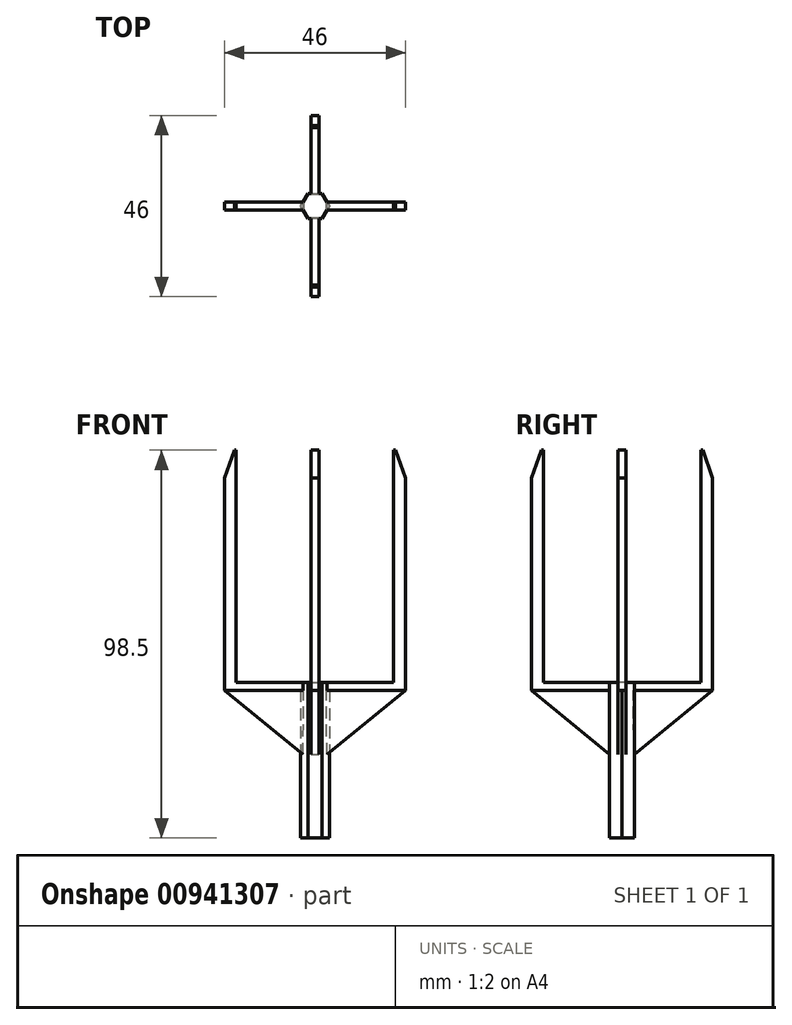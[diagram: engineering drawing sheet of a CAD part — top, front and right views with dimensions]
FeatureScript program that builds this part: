
annotation { "Feature Type Name" : "Feature", "Feature Type Description" : "" }
export const myFeature = defineFeature(function(context is Context, id is Id, definition is map)
    precondition{}
    {
        {
            var Q0;
            Q0=qCreatedBy(makeId("Top.planeOp"),FACE);
            var sketch = newSketch(context, id + "F0", { "sketchPlane" : qUnion([Q0])});
            skCircle(sketch, "E0.cCircle", {"center": v(0, 0) * mm, "radius": 3.15 * mm, "construction": true});
            skLineSegment(sketch, "E0.0", {"start": v(-1.82, 3.15) * mm, "end": v(1.82, 3.15) * mm});
            skLineSegment(sketch, "E0.1", {"start": v(1.82, 3.15) * mm, "end": v(3.64, 0) * mm});
            skLineSegment(sketch, "E0.2", {"start": v(3.64, 0) * mm, "end": v(1.82, -3.15) * mm});
            skLineSegment(sketch, "E0.3", {"start": v(1.82, -3.15) * mm, "end": v(-1.82, -3.15) * mm});
            skLineSegment(sketch, "E0.4", {"start": v(-1.82, -3.15) * mm, "end": v(-3.64, 0) * mm});
            skLineSegment(sketch, "E0.5", {"start": v(-3.64, 0) * mm, "end": v(-1.82, 3.15) * mm});
            skPoint(sketch, "E0.0.midPoint", {"position": v(0, 3.15) * mm});
            skSolve(sketch);
        }
        {
            var Q0;
            Q0=makeQuery(id+"F0.imprint","IMPRINT",FACE,{"disambiguationData":[TD([[makeQuery(id+"F0.imprint","IMPRINT",EDGE,{"derivedFrom":sQuery(id+"F0.wireOp",EDGE,"E0.0")}),-1.0]])]});
            extrude(context, id + "F1", {"entities" : qUnion([Q0]), "depth" : 20 * mm, "offsetDistance" : 25 * mm});
        }
        {
            var Q0;
            Q0=makeQuery(id+"F1.opExtrude","CAP_FACE",FACE,{"disambiguationData":[OSD([sQuery(id+"F0.wireOp",EDGE,"E0.0"),sQuery(id+"F0.wireOp",EDGE,"E0.1"),sQuery(id+"F0.wireOp",EDGE,"E0.2"),sQuery(id+"F0.wireOp",EDGE,"E0.3"),sQuery(id+"F0.wireOp",EDGE,"E0.4"),sQuery(id+"F0.wireOp",EDGE,"E0.5")])],"isStart":false});
            var sketch = newSketch(context, id + "F2", { "sketchPlane" : qUnion([Q0])});
            skLineSegment(sketch, "E1", {"start": v(0, 0) * mm, "end": v(-23, 0) * mm});
            skLineSegment(sketch, "E2", {"start": v(0, 0) * mm, "end": v(21, 0) * mm});
            skLineSegment(sketch, "E3", {"start": v(0, 0) * mm, "end": v(0, 21) * mm});
            skLineSegment(sketch, "E4", {"start": v(0, 0) * mm, "end": v(0, -21) * mm});
            skLineSegment(sketch, "E5.top", {"start": v(0, -1) * mm, "end": v(-23, -1) * mm});
            skLineSegment(sketch, "E5.left", {"start": v(0, 0) * mm, "end": v(0, -1) * mm});
            skLineSegment(sketch, "E5.right", {"start": v(-23, 0) * mm, "end": v(-23, -1) * mm});
            skLineSegment(sketch, "E6.bottom", {"start": v(-23, 0) * mm, "end": v(0, 0) * mm});
            skLineSegment(sketch, "E6.top", {"start": v(-23, 1) * mm, "end": v(0, 1) * mm});
            skLineSegment(sketch, "E6.left", {"start": v(-23, 0) * mm, "end": v(-23, 1) * mm});
            skLineSegment(sketch, "E6.right", {"start": v(0, 0) * mm, "end": v(0, 1) * mm});
            skLineSegment(sketch, "E7.1.0", {"start": v(0, 0) * mm, "end": v(0, -23) * mm});
            skLineSegment(sketch, "E7.1.1", {"start": v(0, -23) * mm, "end": v(-1, -23) * mm});
            skLineSegment(sketch, "E7.1.2", {"start": v(1, 0) * mm, "end": v(1, -23) * mm});
            skLineSegment(sketch, "E7.1.3", {"start": v(0, -23) * mm, "end": v(1, -23) * mm});
            skLineSegment(sketch, "E7.1.4", {"start": v(0, 0) * mm, "end": v(1, 0) * mm});
            skLineSegment(sketch, "E7.1.5", {"start": v(-1, -23) * mm, "end": v(-1, 0) * mm});
            skLineSegment(sketch, "E7.1.6", {"start": v(0, 0) * mm, "end": v(-1, 0) * mm});
            skLineSegment(sketch, "E7.1.7", {"start": v(0, -23) * mm, "end": v(0, 0) * mm});
            skLineSegment(sketch, "E7.1.8", {"start": v(0, 0) * mm, "end": v(0, -23) * mm});
            skLineSegment(sketch, "E7.2.0", {"start": v(0, 0) * mm, "end": v(23, 0) * mm});
            skLineSegment(sketch, "E7.2.1", {"start": v(23, 0) * mm, "end": v(23, -1) * mm});
            skLineSegment(sketch, "E7.2.2", {"start": v(0, 1) * mm, "end": v(23, 1) * mm});
            skLineSegment(sketch, "E7.2.3", {"start": v(23, 0) * mm, "end": v(23, 1) * mm});
            skLineSegment(sketch, "E7.2.5", {"start": v(23, -1) * mm, "end": v(0, -1) * mm});
            skLineSegment(sketch, "E7.2.7", {"start": v(23, 0) * mm, "end": v(0, 0) * mm});
            skLineSegment(sketch, "E7.2.8", {"start": v(0, 0) * mm, "end": v(23, 0) * mm});
            skLineSegment(sketch, "E7.3.0", {"start": v(0, 0) * mm, "end": v(0, 23) * mm});
            skLineSegment(sketch, "E7.3.1", {"start": v(0, 23) * mm, "end": v(1, 23) * mm});
            skLineSegment(sketch, "E7.3.2", {"start": v(-1, 0) * mm, "end": v(-1, 23) * mm});
            skLineSegment(sketch, "E7.3.3", {"start": v(0, 23) * mm, "end": v(-1, 23) * mm});
            skLineSegment(sketch, "E7.3.4", {"start": v(0, 0) * mm, "end": v(-1, 0) * mm});
            skLineSegment(sketch, "E7.3.5", {"start": v(1, 23) * mm, "end": v(1, 0) * mm});
            skLineSegment(sketch, "E7.3.6", {"start": v(0, 0) * mm, "end": v(1, 0) * mm});
            skLineSegment(sketch, "E7.3.7", {"start": v(0, 23) * mm, "end": v(0, 0) * mm});
            skLineSegment(sketch, "E7.3.8", {"start": v(0, 0) * mm, "end": v(0, 23) * mm});
            skPoint(sketch, "E7.center", {"position": v(0, 0) * mm});
            skSolve(sketch);
        }
        {
            var Q0;
            {var subQ4=sQuery(id+"F2.wireOp",EDGE,"E7.3.0");Q0=makeQuery(id+"F2.imprint","IMPRINT",FACE,{"disambiguationData":[TD([[makeQuery(id+"F2.imprint","IMPRINT",EDGE,{"derivedFrom":subQ4}),-1.0]])]});}
            var Q1;
            {var subQ4=sQuery(id+"F2.wireOp",EDGE,"E7.3.0");Q1=makeQuery(id+"F2.imprint","IMPRINT",FACE,{"disambiguationData":[TD([[makeQuery(id+"F2.imprint","IMPRINT",EDGE,{"derivedFrom":subQ4}),1.0]])]});}
            var Q2;
            {var subQ4=sQuery(id+"F2.wireOp",EDGE,"E7.2.0");Q2=makeQuery(id+"F2.imprint","IMPRINT",FACE,{"disambiguationData":[TD([[makeQuery(id+"F2.imprint","IMPRINT",EDGE,{"derivedFrom":subQ4}),1.0]])]});}
            var Q3;
            {var subQ6=sQuery(id+"F2.wireOp",EDGE,"E7.2.0");Q3=makeQuery(id+"F2.imprint","IMPRINT",FACE,{"disambiguationData":[TD([[makeQuery(id+"F2.imprint","IMPRINT",EDGE,{"derivedFrom":subQ6}),-1.0]])]});}
            var Q4;
            {var subQ4=sQuery(id+"F2.wireOp",EDGE,"E7.1.0");Q4=makeQuery(id+"F2.imprint","IMPRINT",FACE,{"disambiguationData":[TD([[makeQuery(id+"F2.imprint","IMPRINT",EDGE,{"derivedFrom":subQ4}),1.0]])]});}
            var Q5;
            {var subQ4=sQuery(id+"F2.wireOp",EDGE,"E7.1.0");Q5=makeQuery(id+"F2.imprint","IMPRINT",FACE,{"disambiguationData":[TD([[makeQuery(id+"F2.imprint","IMPRINT",EDGE,{"derivedFrom":subQ4}),-1.0]])]});}
            var Q6;
            {var subQ3=sQuery(id+"F2.wireOp",EDGE,"E6.left");Q6=makeQuery(id+"F2.imprint","IMPRINT",FACE,{"disambiguationData":[TD([[makeQuery(id+"F2.imprint","IMPRINT",EDGE,{"derivedFrom":subQ3}),-1.0]])]});}
            var Q7;
            {var subQ3=sQuery(id+"F2.wireOp",EDGE,"E5.right");Q7=makeQuery(id+"F2.imprint","IMPRINT",FACE,{"disambiguationData":[TD([[makeQuery(id+"F2.imprint","IMPRINT",EDGE,{"derivedFrom":subQ3}),1.0]])]});}
            var Q8;
            {var subQ0=sQuery(id+"F2.wireOp",EDGE,"E7.3.2");var subQ1=sQuery(id+"F2.wireOp",EDGE,"E6.top");var subQ2=makeQuery(id+"F2.imprint","INTERSECT",VERTEX,{"derivedFrom":[subQ1,subQ0]});Q8=makeQuery(id+"F2.imprint","IMPRINT",FACE,{"disambiguationData":[TD([[makeQuery(id+"F2.imprint","IMPRINT",EDGE,{"disambiguationData":[TD([[subQ2,1.0]])],"derivedFrom":subQ1}),1.0]])]});}
            var Q9;
            {var subQ0=sQuery(id+"F2.wireOp",EDGE,"E6.top");var subQ5=sQuery(id+"F2.wireOp",EDGE,"E7.3.2");var subQ6=makeQuery(id+"F2.imprint","INTERSECT",VERTEX,{"derivedFrom":[subQ0,subQ5]});Q9=makeQuery(id+"F2.imprint","IMPRINT",FACE,{"disambiguationData":[TD([[makeQuery(id+"F2.imprint","IMPRINT",EDGE,{"disambiguationData":[TD([[subQ6,-1.0]])],"derivedFrom":subQ5}),-1.0]])]});}
            var Q10;
            {var subQ0=sQuery(id+"F2.wireOp",EDGE,"E7.2.2");var subQ5=sQuery(id+"F2.wireOp",EDGE,"E7.3.5");var subQ6=makeQuery(id+"F2.imprint","INTERSECT",VERTEX,{"derivedFrom":[subQ0,subQ5]});Q10=makeQuery(id+"F2.imprint","IMPRINT",FACE,{"disambiguationData":[TD([[makeQuery(id+"F2.imprint","IMPRINT",EDGE,{"disambiguationData":[TD([[subQ6,1.0]])],"derivedFrom":subQ5}),-1.0]])]});}
            var Q11;
            {var subQ0=sQuery(id+"F2.wireOp",EDGE,"E7.3.5");var subQ1=sQuery(id+"F2.wireOp",EDGE,"E7.2.2");var subQ2=makeQuery(id+"F2.imprint","INTERSECT",VERTEX,{"derivedFrom":[subQ1,subQ0]});Q11=makeQuery(id+"F2.imprint","IMPRINT",FACE,{"disambiguationData":[TD([[makeQuery(id+"F2.imprint","IMPRINT",EDGE,{"disambiguationData":[TD([[subQ2,-1.0]])],"derivedFrom":subQ1}),1.0]])]});}
            var Q12;
            {var subQ3=sQuery(id+"F2.wireOp",EDGE,"E7.3.5");var subQ5=sQuery(id+"F2.wireOp",EDGE,"E7.2.2");var subQ6=makeQuery(id+"F2.imprint","INTERSECT",VERTEX,{"derivedFrom":[subQ5,subQ3]});Q12=makeQuery(id+"F2.imprint","IMPRINT",FACE,{"disambiguationData":[TD([[makeQuery(id+"F2.imprint","IMPRINT",EDGE,{"disambiguationData":[TD([[subQ6,-1.0]])],"derivedFrom":subQ5}),-1.0]])]});}
            var Q13;
            {var subQ3=sQuery(id+"F2.wireOp",EDGE,"E7.1.2");var subQ5=sQuery(id+"F2.wireOp",EDGE,"E7.2.5");var subQ6=makeQuery(id+"F2.imprint","INTERSECT",VERTEX,{"derivedFrom":[subQ3,subQ5]});Q13=makeQuery(id+"F2.imprint","IMPRINT",FACE,{"disambiguationData":[TD([[makeQuery(id+"F2.imprint","IMPRINT",EDGE,{"disambiguationData":[TD([[subQ6,1.0]])],"derivedFrom":subQ5}),-1.0]])]});}
            var Q14;
            {var subQ0=sQuery(id+"F2.wireOp",EDGE,"E7.2.5");var subQ1=sQuery(id+"F2.wireOp",EDGE,"E7.1.2");var subQ2=makeQuery(id+"F2.imprint","INTERSECT",VERTEX,{"derivedFrom":[subQ1,subQ0]});Q14=makeQuery(id+"F2.imprint","IMPRINT",FACE,{"disambiguationData":[TD([[makeQuery(id+"F2.imprint","IMPRINT",EDGE,{"disambiguationData":[TD([[subQ2,-1.0]])],"derivedFrom":subQ1}),1.0]])]});}
            var Q15;
            {var subQ0=sQuery(id+"F2.wireOp",EDGE,"E7.2.5");var subQ5=sQuery(id+"F2.wireOp",EDGE,"E7.1.2");var subQ6=makeQuery(id+"F2.imprint","INTERSECT",VERTEX,{"derivedFrom":[subQ5,subQ0]});Q15=makeQuery(id+"F2.imprint","IMPRINT",FACE,{"disambiguationData":[TD([[makeQuery(id+"F2.imprint","IMPRINT",EDGE,{"disambiguationData":[TD([[subQ6,-1.0]])],"derivedFrom":subQ5}),-1.0]])]});}
            var Q16;
            {var subQ0=sQuery(id+"F2.wireOp",EDGE,"E5.top");var subQ5=sQuery(id+"F2.wireOp",EDGE,"E7.1.5");var subQ6=makeQuery(id+"F2.imprint","INTERSECT",VERTEX,{"derivedFrom":[subQ0,subQ5]});Q16=makeQuery(id+"F2.imprint","IMPRINT",FACE,{"disambiguationData":[TD([[makeQuery(id+"F2.imprint","IMPRINT",EDGE,{"disambiguationData":[TD([[subQ6,1.0]])],"derivedFrom":subQ5}),-1.0]])]});}
            var Q17;
            {var subQ0=sQuery(id+"F2.wireOp",EDGE,"E7.1.5");var subQ1=sQuery(id+"F2.wireOp",EDGE,"E5.top");var subQ2=makeQuery(id+"F2.imprint","INTERSECT",VERTEX,{"derivedFrom":[subQ1,subQ0]});Q17=makeQuery(id+"F2.imprint","IMPRINT",FACE,{"disambiguationData":[TD([[makeQuery(id+"F2.imprint","IMPRINT",EDGE,{"disambiguationData":[TD([[subQ2,-1.0]])],"derivedFrom":subQ1}),1.0]])]});}
            var Q18;
            {var subQ3=sQuery(id+"F2.wireOp",EDGE,"E7.1.5");var subQ5=sQuery(id+"F2.wireOp",EDGE,"E5.top");var subQ6=makeQuery(id+"F2.imprint","INTERSECT",VERTEX,{"derivedFrom":[subQ5,subQ3]});Q18=makeQuery(id+"F2.imprint","IMPRINT",FACE,{"disambiguationData":[TD([[makeQuery(id+"F2.imprint","IMPRINT",EDGE,{"disambiguationData":[TD([[subQ6,-1.0]])],"derivedFrom":subQ5}),-1.0]])]});}
            var Q19;
            {var subQ3=sQuery(id+"F2.wireOp",EDGE,"E7.3.2");var subQ5=sQuery(id+"F2.wireOp",EDGE,"E6.top");var subQ6=makeQuery(id+"F2.imprint","INTERSECT",VERTEX,{"derivedFrom":[subQ5,subQ3]});Q19=makeQuery(id+"F2.imprint","IMPRINT",FACE,{"disambiguationData":[TD([[makeQuery(id+"F2.imprint","IMPRINT",EDGE,{"disambiguationData":[TD([[subQ6,1.0]])],"derivedFrom":subQ5}),-1.0]])]});}
            var Q20;
            {var subQ0=sQuery(id+"F2.wireOp",EDGE,"E7.3.2");var subQ5=sQuery(id+"F2.wireOp",EDGE,"E6.top");var subQ7=makeQuery(id+"F2.imprint","INTERSECT",VERTEX,{"derivedFrom":[subQ5,subQ0]});Q20=makeQuery(id+"F2.imprint","IMPRINT",FACE,{"disambiguationData":[TD([[makeQuery(id+"F2.imprint","IMPRINT",EDGE,{"disambiguationData":[TD([[subQ7,-1.0]])],"derivedFrom":subQ5}),-1.0]])]});}
            var Q21;
            {var subQ0=sQuery(id+"F2.wireOp",EDGE,"E7.3.5");var subQ5=sQuery(id+"F2.wireOp",EDGE,"E7.2.2");var subQ6=makeQuery(id+"F2.imprint","INTERSECT",VERTEX,{"derivedFrom":[subQ5,subQ0]});Q21=makeQuery(id+"F2.imprint","IMPRINT",FACE,{"disambiguationData":[TD([[makeQuery(id+"F2.imprint","IMPRINT",EDGE,{"disambiguationData":[TD([[subQ6,1.0]])],"derivedFrom":subQ5}),-1.0]])]});}
            var Q22;
            {var subQ0=sQuery(id+"F2.wireOp",EDGE,"E7.1.2");var subQ5=sQuery(id+"F2.wireOp",EDGE,"E7.2.5");var subQ7=makeQuery(id+"F2.imprint","INTERSECT",VERTEX,{"derivedFrom":[subQ0,subQ5]});Q22=makeQuery(id+"F2.imprint","IMPRINT",FACE,{"disambiguationData":[TD([[makeQuery(id+"F2.imprint","IMPRINT",EDGE,{"disambiguationData":[TD([[subQ7,1.0]])],"derivedFrom":subQ0}),-1.0]])]});}
            var Q23;
            {var subQ0=sQuery(id+"F2.wireOp",EDGE,"E7.1.5");var subQ5=sQuery(id+"F2.wireOp",EDGE,"E5.top");var subQ6=makeQuery(id+"F2.imprint","INTERSECT",VERTEX,{"derivedFrom":[subQ5,subQ0]});Q23=makeQuery(id+"F2.imprint","IMPRINT",FACE,{"disambiguationData":[TD([[makeQuery(id+"F2.imprint","IMPRINT",EDGE,{"disambiguationData":[TD([[subQ6,1.0]])],"derivedFrom":subQ5}),-1.0]])]});}
            extrude(context, id + "F3", {"entities" : qUnion([Q0, Q1, Q2, Q3, Q4, Q5, Q6, Q7, Q8, Q9, Q10, Q11, Q12, Q13, Q14, Q15, Q16, Q17, Q18, Q19, Q20, Q21, Q22, Q23]), "operationType" : NewBodyOperationType.ADD, "depth" : 2 * mm, "offsetDistance" : 25 * mm});
        }
        {
            var Q0;
            Q0=makeQuery(id+"F3.opExtrude","CAP_FACE",FACE,{"disambiguationData":[OSD([sQuery(id+"F0.wireOp",EDGE,"E0.0"),sQuery(id+"F0.wireOp",EDGE,"E0.1"),sQuery(id+"F0.wireOp",EDGE,"E0.2"),sQuery(id+"F0.wireOp",EDGE,"E0.3"),sQuery(id+"F0.wireOp",EDGE,"E0.4"),sQuery(id+"F0.wireOp",EDGE,"E0.5"),sQuery(id+"F2.wireOp",EDGE,"E5.top"),sQuery(id+"F2.wireOp",EDGE,"E5.right"),sQuery(id+"F2.wireOp",EDGE,"E6.top"),sQuery(id+"F2.wireOp",EDGE,"E6.left"),sQuery(id+"F2.wireOp",EDGE,"E7.1.1"),sQuery(id+"F2.wireOp",EDGE,"E7.1.2"),sQuery(id+"F2.wireOp",EDGE,"E7.1.3"),sQuery(id+"F2.wireOp",EDGE,"E7.1.5"),sQuery(id+"F2.wireOp",EDGE,"E7.2.1"),sQuery(id+"F2.wireOp",EDGE,"E7.2.2"),sQuery(id+"F2.wireOp",EDGE,"E7.2.3"),sQuery(id+"F2.wireOp",EDGE,"E7.2.5"),sQuery(id+"F2.wireOp",EDGE,"E7.3.1"),sQuery(id+"F2.wireOp",EDGE,"E7.3.2"),sQuery(id+"F2.wireOp",EDGE,"E7.3.3"),sQuery(id+"F2.wireOp",EDGE,"E7.3.5")])],"isStart":false});
            var sketch = newSketch(context, id + "F4", { "sketchPlane" : qUnion([Q0])});
            skLineSegment(sketch, "E8.bottom", {"start": v(-23, 1) * mm, "end": v(-20, 1) * mm});
            skLineSegment(sketch, "E8.top", {"start": v(-23, -1) * mm, "end": v(-20, -1) * mm});
            skLineSegment(sketch, "E8.left", {"start": v(-23, 1) * mm, "end": v(-23, -1) * mm});
            skLineSegment(sketch, "E8.right", {"start": v(-20, 1) * mm, "end": v(-20, -1) * mm});
            skLineSegment(sketch, "E9.bottom", {"start": v(-1, -23) * mm, "end": v(1, -23) * mm});
            skLineSegment(sketch, "E9.top", {"start": v(-1, -20) * mm, "end": v(1, -20) * mm});
            skLineSegment(sketch, "E9.left", {"start": v(-1, -23) * mm, "end": v(-1, -20) * mm});
            skLineSegment(sketch, "E9.right", {"start": v(1, -23) * mm, "end": v(1, -20) * mm});
            skLineSegment(sketch, "E10.bottom", {"start": v(23, 1) * mm, "end": v(20, 1) * mm});
            skLineSegment(sketch, "E10.top", {"start": v(23, -1) * mm, "end": v(20, -1) * mm});
            skLineSegment(sketch, "E10.left", {"start": v(23, 1) * mm, "end": v(23, -1) * mm});
            skLineSegment(sketch, "E10.right", {"start": v(20, 1) * mm, "end": v(20, -1) * mm});
            skLineSegment(sketch, "E11.bottom", {"start": v(-1, 23) * mm, "end": v(1, 23) * mm});
            skLineSegment(sketch, "E11.top", {"start": v(-1, 20) * mm, "end": v(1, 20) * mm});
            skLineSegment(sketch, "E11.left", {"start": v(-1, 23) * mm, "end": v(-1, 20) * mm});
            skLineSegment(sketch, "E11.right", {"start": v(1, 23) * mm, "end": v(1, 20) * mm});
            skSolve(sketch);
        }
        {
            var Q0;
            Q0=makeQuery(id+"F4.imprint","IMPRINT",FACE,{"disambiguationData":[TD([[makeQuery(id+"F4.imprint","IMPRINT",EDGE,{"derivedFrom":sQuery(id+"F4.wireOp",EDGE,"E11.bottom")}),-1.0]])]});
            var Q1;
            Q1=makeQuery(id+"F4.imprint","IMPRINT",FACE,{"disambiguationData":[TD([[makeQuery(id+"F4.imprint","IMPRINT",EDGE,{"derivedFrom":sQuery(id+"F4.wireOp",EDGE,"E8.bottom")}),-1.0]])]});
            var Q2;
            Q2=makeQuery(id+"F4.imprint","IMPRINT",FACE,{"disambiguationData":[TD([[makeQuery(id+"F4.imprint","IMPRINT",EDGE,{"derivedFrom":sQuery(id+"F4.wireOp",EDGE,"E10.bottom")}),-1.0]])]});
            var Q3;
            Q3=makeQuery(id+"F4.imprint","IMPRINT",FACE,{"disambiguationData":[TD([[makeQuery(id+"F4.imprint","IMPRINT",EDGE,{"derivedFrom":sQuery(id+"F4.wireOp",EDGE,"E9.bottom")}),1.0]])]});
            extrude(context, id + "F5", {"entities" : qUnion([Q0, Q1, Q2, Q3]), "operationType" : NewBodyOperationType.ADD, "depth" : 59 * mm, "offsetDistance" : 25 * mm});
        }
        {
            var Q0;
            Q0=makeQuery(id+"F5.opExtrude","CAP_EDGE",EDGE,{"disambiguationData":[OSD([sQuery(id+"F4.wireOp",EDGE,"E11.bottom")])],"isStart":false});
            var Q1;
            Q1=makeQuery(id+"F5.opExtrude","CAP_EDGE",EDGE,{"disambiguationData":[OSD([sQuery(id+"F4.wireOp",EDGE,"E8.left")])],"isStart":false});
            chamfer(context, id + "F6", {"entities" : qUnion([Q0, Q1]), "chamferType" : ChamferType.TWO_OFFSETS, "width1" : 7 * mm, "oppositeDirection" : false, "width2" : 2.5 * mm, "tangentPropagation" : true});
        }
        {
            var Q0;
            Q0=makeQuery(id+"F5.opExtrude","CAP_EDGE",EDGE,{"disambiguationData":[OSD([sQuery(id+"F4.wireOp",EDGE,"E9.bottom")])],"isStart":false});
            var Q1;
            Q1=makeQuery(id+"F5.opExtrude","CAP_EDGE",EDGE,{"disambiguationData":[OSD([sQuery(id+"F4.wireOp",EDGE,"E10.left")])],"isStart":false});
            chamfer(context, id + "F7", {"entities" : qUnion([Q0, Q1]), "chamferType" : ChamferType.TWO_OFFSETS, "width1" : 2.5 * mm, "oppositeDirection" : false, "width2" : 7 * mm, "tangentPropagation" : true});
        }
        {
            var Q0;
            Q0=makeQuery(id+"F5.boolean.opBoolean","MERGE",FACE,{"derivedFrom":[makeQuery(id+"F3.opExtrude","SWEPT_FACE",FACE,{"disambiguationData":[OSD([sQuery(id+"F2.wireOp",EDGE,"E7.1.2")])]}),makeQuery(id+"F5.opExtrude","SWEPT_FACE",FACE,{"disambiguationData":[OSD([sQuery(id+"F4.wireOp",EDGE,"E9.right")])]})]});
            var sketch = newSketch(context, id + "F8", { "sketchPlane" : qUnion([Q0])});
            skLineSegment(sketch, "E12", {"start": v(-23, 20) * mm, "end": v(-3.03, 3.67) * mm});
            skLineSegment(sketch, "E13", {"start": v(-3.03, 3.67) * mm, "end": v(-2.89, 20) * mm});
            skLineSegment(sketch, "E14", {"start": v(-2.89, 20) * mm, "end": v(-23, 20) * mm});
            skSolve(sketch);
        }
        {
            var Q0;
            {var subQ0=sQuery(id+"F8.wireOp",EDGE,"E12");Q0=makeQuery(id+"F8.imprint","IMPRINT",FACE,{"disambiguationData":[TD([[makeQuery(id+"F8.imprint","IMPRINT",EDGE,{"derivedFrom":subQ0}),1.0]])]});}
            extrude(context, id + "F9", {"entities" : qUnion([Q0]), "oppositeDirection" : true, "depth" : 2 * mm, "offsetDistance" : 25 * mm});
        }
        {
            var Q0;
            Q0=makeQuery(id+"F1.opExtrude","CAP_FACE",FACE,{"disambiguationData":[OSD([sQuery(id+"F0.wireOp",EDGE,"E0.0"),sQuery(id+"F0.wireOp",EDGE,"E0.1"),sQuery(id+"F0.wireOp",EDGE,"E0.2"),sQuery(id+"F0.wireOp",EDGE,"E0.3"),sQuery(id+"F0.wireOp",EDGE,"E0.4"),sQuery(id+"F0.wireOp",EDGE,"E0.5")])],"isStart":true});
            extrude(context, id + "F10", {"entities" : qUnion([Q0]), "operationType" : NewBodyOperationType.ADD, "depth" : 17.5 * mm, "offsetDistance" : 25 * mm});
        }
        {
            var Q0;
            Q0=qCreatedBy(makeId("Right.planeOp"),FACE);
            var sketch = newSketch(context, id + "F11", { "sketchPlane" : qUnion([Q0])});
            skLineSegment(sketch, "E15", {"start": v(0, 0) * mm, "end": v(0, 104.62) * mm});
            skSolve(sketch);
        }
        {
            var Q0;
            Q0=makeQuery(id+"F9.opExtrude","SWEPT_BODY",BODY,{"disambiguationData":[OSD([sQuery(id+"F8.wireOp",EDGE,"E12"),sQuery(id+"F8.wireOp",EDGE,"E13"),sQuery(id+"F8.wireOp",EDGE,"E14")])]});
            var Q1;
            Q1=sQuery(id+"F11.wireOp",EDGE,"E15");
            circularPattern(context, id + "F12", {"entities" : qUnion([Q0]), "axis" : qUnion([Q1]), "angle" : 360 * degree, "instanceCount" : 4, "equalSpace" : true});
        }
    });
